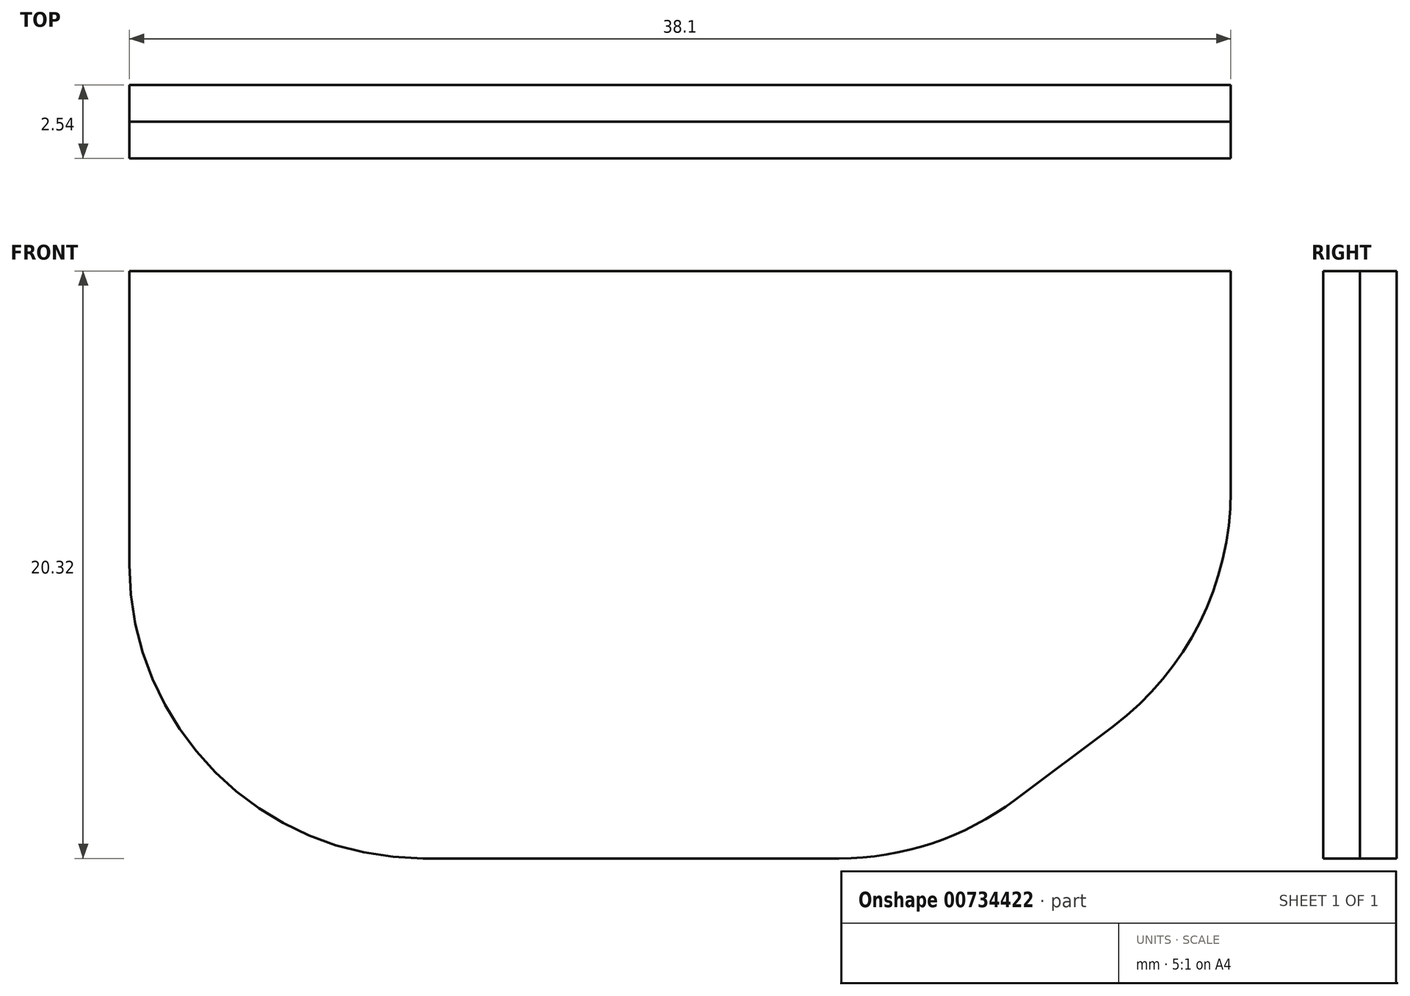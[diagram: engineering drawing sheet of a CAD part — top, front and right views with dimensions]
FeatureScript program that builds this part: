
annotation { "Feature Type Name" : "Feature", "Feature Type Description" : "" }
export const myFeature = defineFeature(function(context is Context, id is Id, definition is map)
    precondition{}
    {
        {
            var Q0;
            Q0=qCreatedBy(makeId("Front.planeOp"),FACE);
            var sketch = newSketch(context, id + "F0", { "sketchPlane" : qUnion([Q0])});
            skLineSegment(sketch, "E0", {"start": v(-47.54, 29.82) * mm, "end": v(-9.44, 29.82) * mm});
            skLineSegment(sketch, "E1", {"start": v(-9.44, 29.82) * mm, "end": v(-9.44, 17.12) * mm});
            skLineSegment(sketch, "E2", {"start": v(-9.44, 17.12) * mm, "end": v(-19.6, 9.5) * mm});
            skLineSegment(sketch, "E3", {"start": v(-19.6, 9.5) * mm, "end": v(-47.54, 9.5) * mm});
            skLineSegment(sketch, "E4", {"start": v(-47.54, 9.5) * mm, "end": v(-47.54, 29.82) * mm});
            skSolve(sketch);
        }
        {
            var Q0;
            Q0 = qSketchRegion(id + "F0", true);
            extrude(context, id + "F1", {"entities" : qUnion([Q0]), "depth" : 1.27 * mm, "offsetDistance" : 25.4 * mm});
        }
        {
            var Q0;
            Q0=makeQuery(id+"F1.opExtrude","SWEPT_EDGE",EDGE,{"disambiguationData":[OSD([sQuery(id+"F0.wireOp",EDGE,"E3"),sQuery(id+"F0.wireOp",EDGE,"E4")])]});
            var Q1;
            Q1=makeQuery(id+"F1.opExtrude","SWEPT_EDGE",EDGE,{"disambiguationData":[OSD([sQuery(id+"F0.wireOp",EDGE,"E2"),sQuery(id+"F0.wireOp",EDGE,"E3")])]});
            var Q2;
            Q2=makeQuery(id+"F1.opExtrude","SWEPT_EDGE",EDGE,{"disambiguationData":[OSD([sQuery(id+"F0.wireOp",EDGE,"E1"),sQuery(id+"F0.wireOp",EDGE,"E2")])]});
            fillet(context, id + "F2", {"entities" : qUnion([Q0, Q1, Q2]), "radius" : 10.16 * mm, "tangentPropagation" : true, "allowEdgeOverflow" : false});
        }
        {
            var Q0;
            Q0=makeQuery(id+"F1.opExtrude","SWEPT_BODY",BODY,{"disambiguationData":[OSD([sQuery(id+"F0.wireOp",EDGE,"E0"),sQuery(id+"F0.wireOp",EDGE,"E1"),sQuery(id+"F0.wireOp",EDGE,"E2"),sQuery(id+"F0.wireOp",EDGE,"E3"),sQuery(id+"F0.wireOp",EDGE,"E4")])]});
            var Q1;
            Q1=qCreatedBy(makeId("Front.planeOp"),FACE);
            mirror(context, id + "F3", {"entities" : qUnion([Q0]), "mirrorPlane" : qUnion([Q1])});
        }
    });
